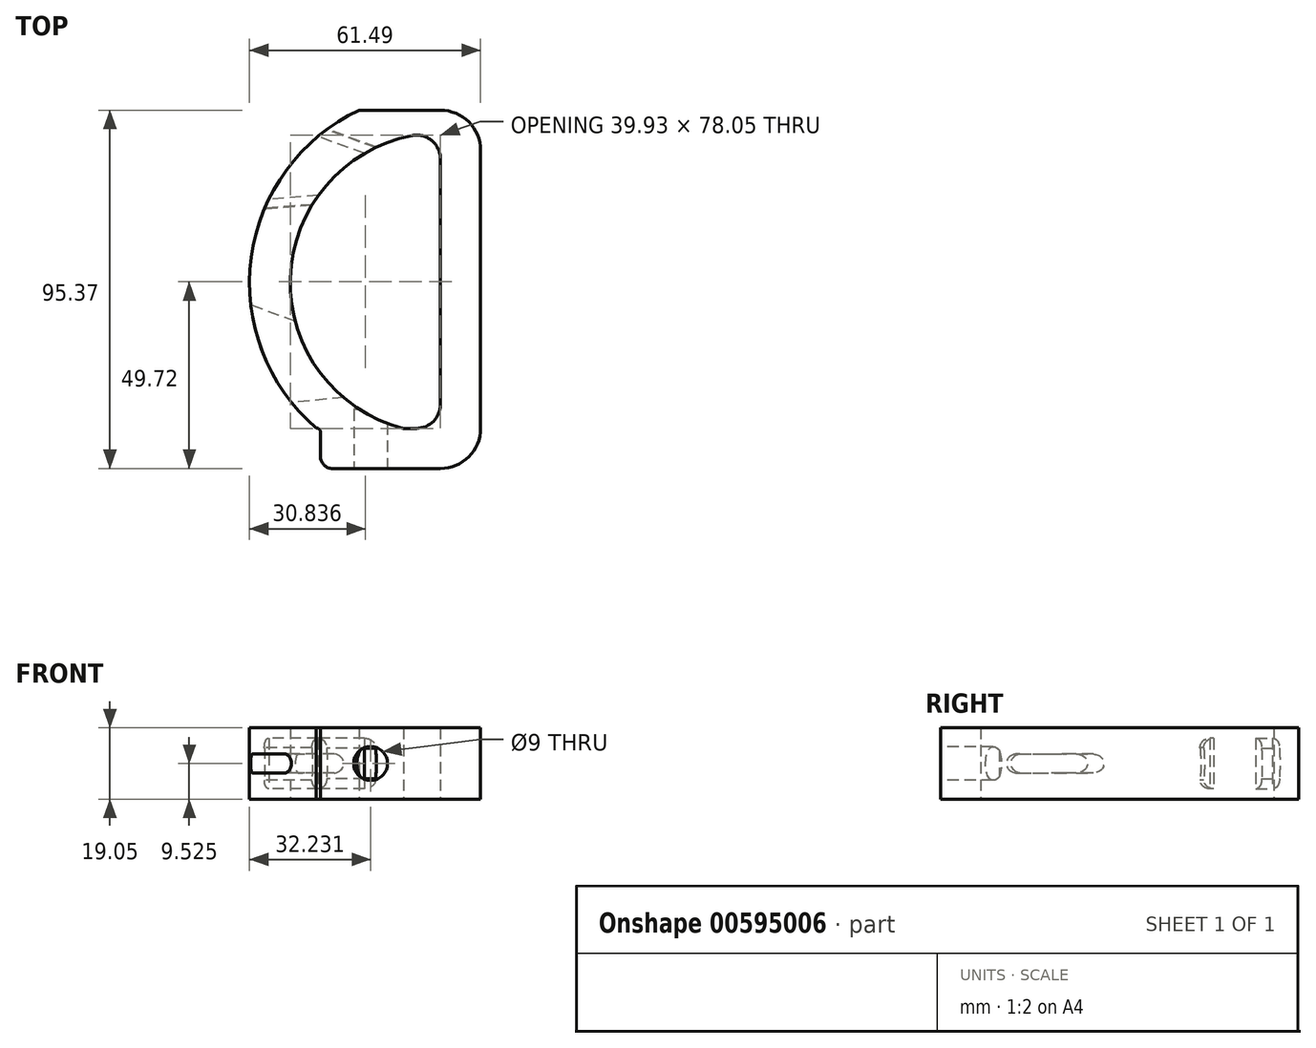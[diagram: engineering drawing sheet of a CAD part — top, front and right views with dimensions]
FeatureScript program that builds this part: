
annotation { "Feature Type Name" : "Feature", "Feature Type Description" : "" }
export const myFeature = defineFeature(function(context is Context, id is Id, definition is map)
    precondition{}
    {
        {
            var Q0;
            Q0=qCreatedBy(makeId("Top.planeOp"),FACE);
            var sketch = newSketch(context, id + "F0", { "sketchPlane" : qUnion([Q0])});
            skArc(sketch, "E0", {"start": v(-21.64, 45.96) * mm, "mid": v(-50.35, 6.76) * mm, "end": v(-33, -38.63) * mm});
            skArc(sketch, "E1", {"start": v(-7.55, 39.23) * mm, "mid": v(-39.93, 1.17) * mm, "end": v(-9.83, -38.72) * mm});
            skLineSegment(sketch, "E2", {"start": v(0, 45.96) * mm, "end": v(-21.64, 45.96) * mm});
            skLineSegment(sketch, "E3", {"start": v(10.69, 35.27) * mm, "end": v(10.69, -38.72) * mm});
            skLineSegment(sketch, "E4", {"start": v(0, 33) * mm, "end": v(0, -32.37) * mm});
            skLineSegment(sketch, "E5", {"start": v(-6.35, -38.72) * mm, "end": v(-9.83, -38.72) * mm});
            skPoint(sketch, "E6", {"position": v(-50.8, 0) * mm});
            skPoint(sketch, "E7", {"position": v(-44.25, -24.96) * mm});
            skPoint(sketch, "E8", {"position": v(-47.9, 16.9) * mm});
            skLineSegment(sketch, "E9", {"start": v(-28.7, -49.4) * mm, "end": v(0, -49.4) * mm});
            skPoint(sketch, "E10.visualSharp", {"position": v(10.69, -49.4) * mm});
            skArc(sketch, "E10.filletArc", {"start": v(0, -49.4) * mm, "mid": v(7.56, -46.28) * mm, "end": v(10.69, -38.72) * mm});
            skPoint(sketch, "E11.visualSharp", {"position": v(10.69, 45.96) * mm});
            skArc(sketch, "E11.filletArc", {"start": v(10.69, 35.27) * mm, "mid": v(7.56, 42.83) * mm, "end": v(0, 45.96) * mm});
            skPoint(sketch, "E12.visualSharp", {"position": v(0, 39.95) * mm});
            skArc(sketch, "E12.filletArc", {"start": v(0, 33) * mm, "mid": v(-2.3, 37.89) * mm, "end": v(-7.55, 39.23) * mm});
            skArc(sketch, "E13.filletArc", {"start": v(-6.35, -38.72) * mm, "mid": v(-1.86, -36.86) * mm, "end": v(0, -32.37) * mm});
            skPoint(sketch, "E14", {"position": v(-50.65, -3.9) * mm});
            skPoint(sketch, "E15", {"position": v(-36.28, 35.56) * mm});
            skLineSegment(sketch, "E16", {"start": v(-31.92, -46.18) * mm, "end": v(-31.92, -39.7) * mm});
            skLineSegment(sketch, "E17", {"start": v(-33, -38.63) * mm, "end": v(-33, -38.63) * mm});
            skPoint(sketch, "E18.visualSharp", {"position": v(-31.92, -38.63) * mm});
            skArc(sketch, "E18.filletArc", {"start": v(-31.92, -39.7) * mm, "mid": v(-32.23, -38.94) * mm, "end": v(-33, -38.63) * mm});
            skPoint(sketch, "E19.visualSharp", {"position": v(-31.92, -49.4) * mm});
            skArc(sketch, "E19.filletArc", {"start": v(-31.92, -46.18) * mm, "mid": v(-30.98, -48.46) * mm, "end": v(-28.7, -49.4) * mm});
            skSolve(sketch);
        }
        {
            var Q0;
            Q0=makeQuery(id+"F0.imprint","IMPRINT",FACE,{"disambiguationData":[TD([[makeQuery(id+"F0.imprint","IMPRINT",EDGE,{"derivedFrom":sQuery(id+"F0.wireOp",EDGE,"E0")}),1.0]])]});
            extrude(context, id + "F1", {"entities" : qUnion([Q0]), "depth" : 19.05 * mm, "offsetDistance" : 25.4 * mm});
        }
        {
            var Q0;
            Q0=makeQuery(id+"F1.opExtrude","SWEPT_FACE",FACE,{"disambiguationData":[OSD([sQuery(id+"F0.wireOp",EDGE,"E4")])]});
            cPlane(context, id + "F2", {"entities" : qUnion([Q0]), "cplaneType" : CPlaneType.OFFSET, "offset" : 50.8 * mm, "width" : 152.4 * mm, "height" : 152.4 * mm});
        }
        {
            var Q0;
            Q0=makeQuery(id+"F1.opExtrude","SWEPT_FACE",FACE,{"disambiguationData":[OSD([sQuery(id+"F0.wireOp",EDGE,"E9")])]});
            var sketch = newSketch(context, id + "F3", { "sketchPlane" : qUnion([Q0])});
            skPoint(sketch, "E20", {"position": v(-18.57, 9.53) * mm});
            skSolve(sketch);
        }
        {
            var Q0;
            Q0=sQuery(id+"F3.wireOp",VERTEX,"E20");
            var Q1;
            Q1=makeQuery(id+"F1.opExtrude","SWEPT_BODY",BODY,{"disambiguationData":[OSD([sQuery(id+"F0.wireOp",EDGE,"E0"),sQuery(id+"F0.wireOp",EDGE,"E1"),sQuery(id+"F0.wireOp",EDGE,"E2"),sQuery(id+"F0.wireOp",EDGE,"E3"),sQuery(id+"F0.wireOp",EDGE,"dOx9RUUg-dijC-ZvtV-rfcF-Oi3RTDK4aGwI"),sQuery(id+"F0.wireOp",EDGE,"E4"),sQuery(id+"F0.wireOp",EDGE,"E5"),sQuery(id+"F0.wireOp",EDGE,"E9")])]});
            hole(context, id + "F4", {"style" : HoleStyle.SIMPLE, "endStyle" : HoleEndStyle.BLIND, "standardTappedOrClearance" : lookupTablePath({ "standard" : "ISO", "engagement" : "75%", "pitch" : "1 mm", "size" : "M10", "type" : "Tapped" }), "standardBlindInLast" : lookupTablePath({ "standard" : "ISO", "engagement" : "75%", "pitch" : "1 mm", "size" : "M10", "type" : "Tapped" }), "holeDiameter" : 9 * mm, "showTappedDepth" : true, "holeDepth" : 15.7 * mm, "isTappedThrough" : true, "tappedDepth" : 12.7 * mm, "tapClearance" : 3, "locations" : qUnion([Q0]), "scope" : qUnion([Q1]), "majorDiameter" : 10 * mm});
        }
        {
            var Q0;
            Q0=qCreatedBy(id+"F2.planeOp",FACE);
            var sketch = newSketch(context, id + "F5", { "sketchPlane" : qUnion([Q0])});
            skPoint(sketch, "E21", {"position": v(-17.21, 0) * mm});
            skPoint(sketch, "E22", {"position": v(-35.87, 0) * mm});
            skPoint(sketch, "E23", {"position": v(3.6, 0) * mm});
            skPoint(sketch, "E24", {"position": v(24.65, 0) * mm});
            skLineSegment(sketch, "E25", {"start": v(-35.87, 0) * mm, "end": v(-35.87, 19.05) * mm});
            skLineSegment(sketch, "E26", {"start": v(-17.21, 0) * mm, "end": v(-17.21, 19.05) * mm});
            skLineSegment(sketch, "E27", {"start": v(3.6, 0) * mm, "end": v(3.6, 7.02) * mm});
            skLineSegment(sketch, "E28", {"start": v(24.65, 0) * mm, "end": v(24.65, 7.02) * mm});
            skArc(sketch, "E29", {"start": v(-35.87, 16.26) * mm, "mid": v(-37.56, 15.6) * mm, "end": v(-38.36, 13.97) * mm});
            skArc(sketch, "E30.MirrorCS", {"start": v(-35.87, 2.8) * mm, "mid": v(-37.56, 3.45) * mm, "end": v(-38.36, 5.08) * mm});
            skArc(sketch, "E31", {"start": v(-38.36, 13.97) * mm, "mid": v(-38.54, 9.52) * mm, "end": v(-38.36, 5.08) * mm});
            skLineSegment(sketch, "E32", {"start": v(-35.87, 5.3) * mm, "end": v(-35.87, 13.76) * mm});
            skPoint(sketch, "E33", {"position": v(-35.87, 9.52) * mm});
            skLineSegment(sketch, "E34", {"start": v(-1.84, -3.07) * mm, "end": v(-1.84, 15.98) * mm});
            skArc(sketch, "E35", {"start": v(-14.72, 13.55) * mm, "mid": v(-15.37, 15.45) * mm, "end": v(-17.21, 16.26) * mm});
            skArc(sketch, "E36.MirrorCS", {"start": v(-14.72, 5.5) * mm, "mid": v(-15.37, 3.6) * mm, "end": v(-17.21, 2.8) * mm});
            skArc(sketch, "E37", {"start": v(-14.72, 13.55) * mm, "mid": v(-14.89, 9.52) * mm, "end": v(-14.72, 5.5) * mm});
            skLineSegment(sketch, "E38", {"start": v(-17.21, 5.3) * mm, "end": v(-17.21, 13.76) * mm});
            skPoint(sketch, "E39", {"position": v(-17.21, 9.53) * mm});
            skLineSegment(sketch, "E40", {"start": v(-35.87, 2.8) * mm, "end": v(-17.21, 2.8) * mm});
            skLineSegment(sketch, "E41", {"start": v(-35.87, 16.26) * mm, "end": v(-17.21, 16.26) * mm});
            skArc(sketch, "E42", {"start": v(3.6, 12.03) * mm, "mid": v(1.1, 9.52) * mm, "end": v(3.6, 7.02) * mm});
            skArc(sketch, "E43", {"start": v(24.65, 7.02) * mm, "mid": v(27.15, 9.52) * mm, "end": v(24.65, 12.03) * mm});
            skLineSegment(sketch, "E44", {"start": v(3.6, 12.03) * mm, "end": v(24.65, 12.03) * mm});
            skLineSegment(sketch, "E45", {"start": v(3.6, 7.02) * mm, "end": v(24.65, 7.02) * mm});
            skLineSegment(sketch, "E46.trimOffspring", {"start": v(3.6, 12.03) * mm, "end": v(3.6, 19.05) * mm});
            skLineSegment(sketch, "E47.trimOffspring", {"start": v(24.65, 12.03) * mm, "end": v(24.65, 19.05) * mm});
            skSolve(sketch);
        }
        {
            var Q0;
            Q0=sQuery(id+"F5.wireOp",EDGE,"E34");
            cPlane(context, id + "F6", {"entities" : qUnion([Q0]), "cplaneType" : CPlaneType.LINE_ANGLE, "offset" : 25.4 * mm, "angle" : 20 * degree, "oppositeDirection" : true, "width" : 152.4 * mm, "height" : 152.4 * mm});
        }
        {
            var Q0;
            Q0=qCreatedBy(id+"F6.planeOp",FACE);
            cPlane(context, id + "F7", {"entities" : qUnion([Q0]), "cplaneType" : CPlaneType.OFFSET, "offset" : 12.7 * mm, "oppositeDirection" : true, "width" : 152.4 * mm, "height" : 152.4 * mm});
        }
        {
            var Q0;
            Q0=qCreatedBy(id+"F7.planeOp",FACE);
            var sketch = newSketch(context, id + "F8", { "sketchPlane" : qUnion([Q0])});
            skPoint(sketch, "E48", {"position": v(25.47, 0) * mm});
            skLineSegment(sketch, "E49", {"start": v(13.01, 2.8) * mm, "end": v(13.01, 16.26) * mm});
            skLineSegment(sketch, "E50", {"start": v(25.47, 0) * mm, "end": v(25.47, 19.05) * mm});
            skLineSegment(sketch, "E51", {"start": v(13.01, 5.3) * mm, "end": v(13.01, 13.76) * mm});
            skPoint(sketch, "E52", {"position": v(13.01, 9.53) * mm});
            skArc(sketch, "E53", {"start": v(27.97, 13.55) * mm, "mid": v(27.31, 15.45) * mm, "end": v(25.47, 16.26) * mm});
            skArc(sketch, "E54.MirrorCS", {"start": v(27.97, 5.5) * mm, "mid": v(27.31, 3.6) * mm, "end": v(25.47, 2.8) * mm});
            skLineSegment(sketch, "E55", {"start": v(25.47, 5.3) * mm, "end": v(25.47, 13.76) * mm});
            skPoint(sketch, "E56", {"position": v(25.47, 9.53) * mm});
            skLineSegment(sketch, "E57", {"start": v(13.01, 2.8) * mm, "end": v(25.47, 2.8) * mm});
            skLineSegment(sketch, "E58", {"start": v(13.01, 16.26) * mm, "end": v(25.47, 16.26) * mm});
            skArc(sketch, "E59", {"start": v(27.97, 5.5) * mm, "mid": v(28.12, 9.53) * mm, "end": v(27.97, 13.55) * mm});
            skSolve(sketch);
        }
        {
            var Q0;
            Q0=sQuery(id+"F5.wireOp",EDGE,"E34");
            cPlane(context, id + "F9", {"entities" : qUnion([Q0]), "cplaneType" : CPlaneType.LINE_ANGLE, "offset" : 25.4 * mm, "angle" : 4.42 * degree, "width" : 152.4 * mm, "height" : 152.4 * mm});
        }
        {
            var Q0;
            Q0=qCreatedBy(id+"F9.planeOp",FACE);
            cPlane(context, id + "F10", {"entities" : qUnion([Q0]), "cplaneType" : CPlaneType.OFFSET, "offset" : 15.24 * mm, "oppositeDirection" : true, "width" : 152.4 * mm, "height" : 152.4 * mm});
        }
        {
            var Q0;
            Q0=qCreatedBy(id+"F10.planeOp",FACE);
            var sketch = newSketch(context, id + "F11", { "sketchPlane" : qUnion([Q0])});
            skPoint(sketch, "E60", {"position": v(33.33, 0) * mm});
            skPoint(sketch, "E61", {"position": v(25.7, 0) * mm});
            skLineSegment(sketch, "E62", {"start": v(25.7, 0) * mm, "end": v(25.7, 19.05) * mm});
            skLineSegment(sketch, "E63", {"start": v(33.33, 0) * mm, "end": v(33.33, 19.05) * mm});
            skArc(sketch, "E64", {"start": v(25.7, 16.26) * mm, "mid": v(23.93, 15.52) * mm, "end": v(23.2, 13.73) * mm});
            skArc(sketch, "E65.MirrorCS", {"start": v(25.7, 2.8) * mm, "mid": v(24.02, 3.45) * mm, "end": v(23.22, 5.08) * mm});
            skLineSegment(sketch, "E66", {"start": v(25.7, 5.3) * mm, "end": v(25.7, 13.76) * mm});
            skPoint(sketch, "E67", {"position": v(25.7, 9.52) * mm});
            skArc(sketch, "E68", {"start": v(35.82, 13.55) * mm, "mid": v(35.17, 15.45) * mm, "end": v(33.33, 16.26) * mm});
            skArc(sketch, "E69.MirrorCS", {"start": v(35.82, 5.5) * mm, "mid": v(35.17, 3.6) * mm, "end": v(33.33, 2.8) * mm});
            skArc(sketch, "E70", {"start": v(35.82, 13.55) * mm, "mid": v(35.65, 9.52) * mm, "end": v(35.82, 5.5) * mm});
            skLineSegment(sketch, "E71", {"start": v(33.33, 5.3) * mm, "end": v(33.33, 13.76) * mm});
            skPoint(sketch, "E72", {"position": v(33.33, 9.52) * mm});
            skLineSegment(sketch, "E73", {"start": v(25.7, 2.8) * mm, "end": v(33.33, 2.8) * mm});
            skLineSegment(sketch, "E74", {"start": v(25.7, 16.26) * mm, "end": v(33.33, 16.26) * mm});
            skArc(sketch, "E75", {"start": v(23.22, 5.08) * mm, "mid": v(23.4, 9.4) * mm, "end": v(23.2, 13.73) * mm});
            skSolve(sketch);
        }
        {
            var Q0;
            {var subQ1=sQuery(id+"F8.wireOp",EDGE,"E53");Q0=makeQuery(id+"F8.imprint","IMPRINT",FACE,{"disambiguationData":[TD([[makeQuery(id+"F8.imprint","IMPRINT",EDGE,{"derivedFrom":subQ1}),1.0]])]});}
            var Q1;
            {var subQ5=sQuery(id+"F8.wireOp",EDGE,"E51");Q1=makeQuery(id+"F8.imprint","IMPRINT",FACE,{"disambiguationData":[TD([[makeQuery(id+"F8.imprint","IMPRINT",EDGE,{"derivedFrom":subQ5}),-1.0]])]});}
            var Q2;
            {var subQ0=sQuery(id+"F8.wireOp",EDGE,"79d6455e-a1dc-483f-a46f-3cff99740c98");Q2=makeQuery(id+"F8.imprint","IMPRINT",FACE,{"disambiguationData":[TD([[makeQuery(id+"F8.imprint","IMPRINT",EDGE,{"derivedFrom":subQ0}),1.0]])]});}
            extrude(context, id + "F12", {"entities" : qUnion([Q0, Q1, Q2]), "operationType" : NewBodyOperationType.REMOVE, "depth" : 38.1 * mm, "offsetDistance" : 25.4 * mm});
        }
        {
            var Q0;
            {var subQ5=sQuery(id+"F11.wireOp",EDGE,"E66");Q0=makeQuery(id+"F11.imprint","IMPRINT",FACE,{"disambiguationData":[TD([[makeQuery(id+"F11.imprint","IMPRINT",EDGE,{"derivedFrom":subQ5}),-1.0]])]});}
            var Q1;
            {var subQ0=sQuery(id+"F11.wireOp",EDGE,"E64");Q1=makeQuery(id+"F11.imprint","IMPRINT",FACE,{"disambiguationData":[TD([[makeQuery(id+"F11.imprint","IMPRINT",EDGE,{"derivedFrom":subQ0}),1.0]])]});}
            extrude(context, id + "F13", {"entities" : qUnion([Q0, Q1]), "operationType" : NewBodyOperationType.REMOVE, "depth" : 44.45 * mm, "offsetDistance" : 25.4 * mm});
        }
        {
            var Q0;
            Q0=sQuery(id+"F5.wireOp",EDGE,"E34");
            cPlane(context, id + "F14", {"entities" : qUnion([Q0]), "cplaneType" : CPlaneType.LINE_ANGLE, "offset" : 25.4 * mm, "angle" : 20 * degree, "oppositeDirection" : true, "width" : 152.4 * mm, "height" : 152.4 * mm});
        }
        {
            var Q0;
            Q0=qCreatedBy(id+"F14.planeOp",FACE);
            var sketch = newSketch(context, id + "F15", { "sketchPlane" : qUnion([Q0])});
            skArc(sketch, "E76", {"start": v(-25.33, 7.02) * mm, "mid": v(-22.83, 9.52) * mm, "end": v(-25.33, 12.03) * mm});
            skLineSegment(sketch, "E77", {"start": v(-35.49, 12.03) * mm, "end": v(-25.33, 12.03) * mm});
            skLineSegment(sketch, "E78", {"start": v(-35.49, 7.02) * mm, "end": v(-25.33, 7.02) * mm});
            skLineSegment(sketch, "E79", {"start": v(-35.49, 7.02) * mm, "end": v(-35.49, 12.03) * mm});
            skSolve(sketch);
        }
        {
            var Q0;
            Q0=sQuery(id+"F5.wireOp",EDGE,"E34");
            cPlane(context, id + "F16", {"entities" : qUnion([Q0]), "cplaneType" : CPlaneType.LINE_ANGLE, "offset" : 25.4 * mm, "angle" : 5 * degree, "width" : 152.4 * mm, "height" : 152.4 * mm});
        }
        {
            var Q0;
            Q0=qCreatedBy(id+"F16.planeOp",FACE);
            cPlane(context, id + "F17", {"entities" : qUnion([Q0]), "cplaneType" : CPlaneType.OFFSET, "offset" : 38.1 * mm, "oppositeDirection" : true, "width" : 152.4 * mm, "height" : 152.4 * mm});
        }
        {
            var Q0;
            Q0=qCreatedBy(id+"F17.planeOp",FACE);
            var sketch = newSketch(context, id + "F18", { "sketchPlane" : qUnion([Q0])});
            skLineSegment(sketch, "E80.bottom", {"start": v(-12.62, 7.03) * mm, "end": v(-25.7, 7.03) * mm});
            skLineSegment(sketch, "E80.top", {"start": v(-12.62, 12.03) * mm, "end": v(-25.7, 12.03) * mm});
            skArc(sketch, "E81", {"start": v(-25.7, 12.03) * mm, "mid": v(-28.2, 9.53) * mm, "end": v(-25.7, 7.03) * mm});
            skLineSegment(sketch, "E82", {"start": v(-12.62, 12.03) * mm, "end": v(-12.62, 7.03) * mm});
            skSolve(sketch);
        }
        {
            var Q0;
            Q0=makeQuery(id+"F18.imprint","IMPRINT",FACE,{"disambiguationData":[TD([[makeQuery(id+"F18.imprint","IMPRINT",EDGE,{"derivedFrom":sQuery(id+"F18.wireOp",EDGE,"E80.bottom")}),-1.0]])]});
            var Q1;
            Q1=makeQuery(id+"F1.opExtrude","SWEPT_FACE",FACE,{"disambiguationData":[OSD([sQuery(id+"F0.wireOp",EDGE,"E4")])]});
            extrude(context, id + "F19", {"entities" : qUnion([Q0]), "operationType" : NewBodyOperationType.REMOVE, "depth" : 76.2 * mm, "endBoundEntityFace" : qUnion([Q1]), "offsetDistance" : 25.4 * mm});
        }
        {
            var Q0;
            Q0=qSketchRegion(id+"F15",true);
            extrude(context, id + "F20", {"entities" : qUnion([Q0]), "operationType" : NewBodyOperationType.REMOVE, "depth" : 20.32 * mm, "offsetDistance" : 25.4 * mm});
        }
    });
